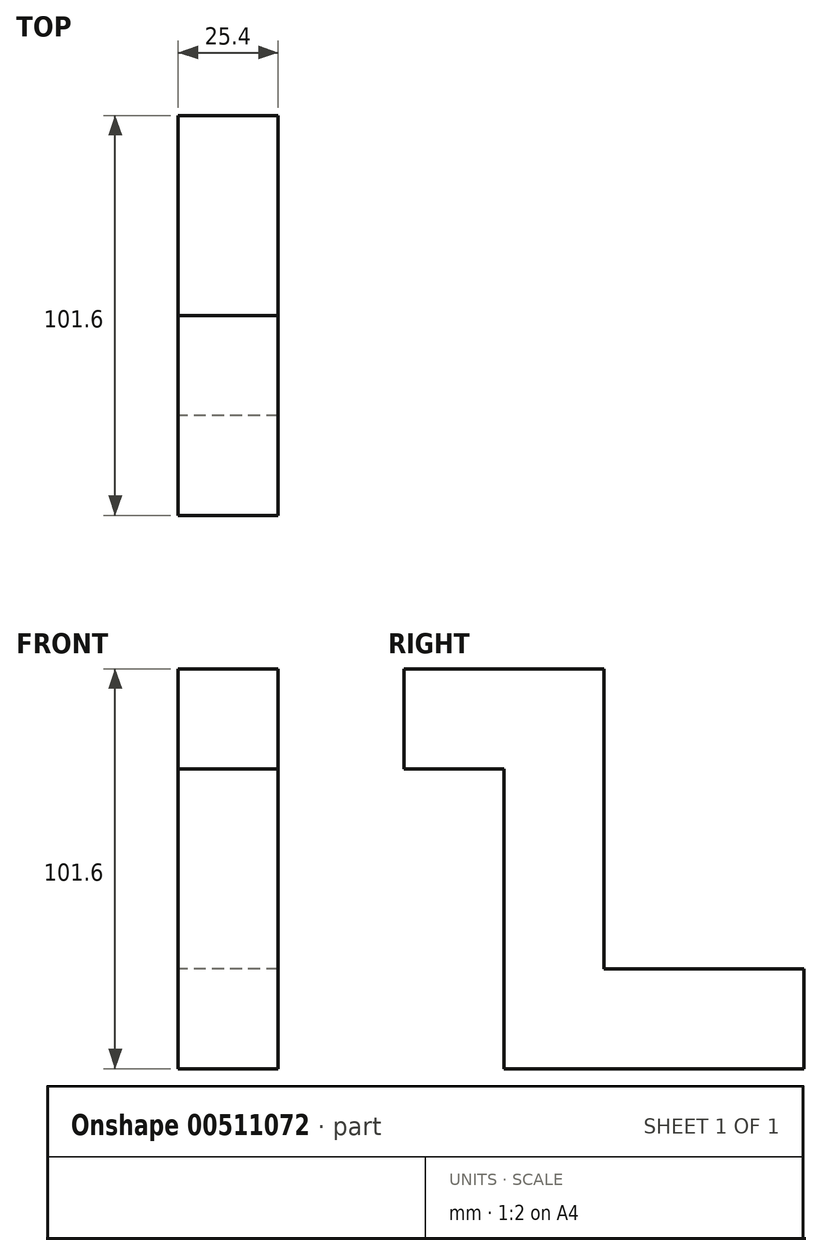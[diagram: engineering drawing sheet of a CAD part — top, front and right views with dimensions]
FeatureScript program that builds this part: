
annotation { "Feature Type Name" : "Feature", "Feature Type Description" : "" }
export const myFeature = defineFeature(function(context is Context, id is Id, definition is map)
    precondition{}
    {
        {
            var Q0;
            Q0=qCreatedBy(makeId("Right.planeOp"),FACE);
            var sketch = newSketch(context, id + "F0", { "sketchPlane" : qUnion([Q0])});
            skLineSegment(sketch, "E0", {"start": v(-44.4, 47.61) * mm, "end": v(6.4, 47.61) * mm});
            skLineSegment(sketch, "E1", {"start": v(6.4, 47.61) * mm, "end": v(6.4, -28.59) * mm});
            skLineSegment(sketch, "E2", {"start": v(6.4, -28.59) * mm, "end": v(57.2, -28.59) * mm});
            skLineSegment(sketch, "E3", {"start": v(57.2, -28.59) * mm, "end": v(57.2, -53.99) * mm});
            skLineSegment(sketch, "E4", {"start": v(57.2, -53.99) * mm, "end": v(-19, -53.99) * mm});
            skLineSegment(sketch, "E5", {"start": v(-19, -53.99) * mm, "end": v(-19, 22.21) * mm});
            skLineSegment(sketch, "E6", {"start": v(-19, 22.21) * mm, "end": v(-44.4, 22.21) * mm});
            skLineSegment(sketch, "E7", {"start": v(-44.4, 22.21) * mm, "end": v(-44.4, 47.61) * mm});
            skSolve(sketch);
        }
        {
            var Q0;
            Q0 = qSketchRegion(id + "F0", true);
            extrude(context, id + "F1", {"entities" : qUnion([Q0]), "depth" : 25.4 * mm, "offsetDistance" : 25.4 * mm});
        }
    });
